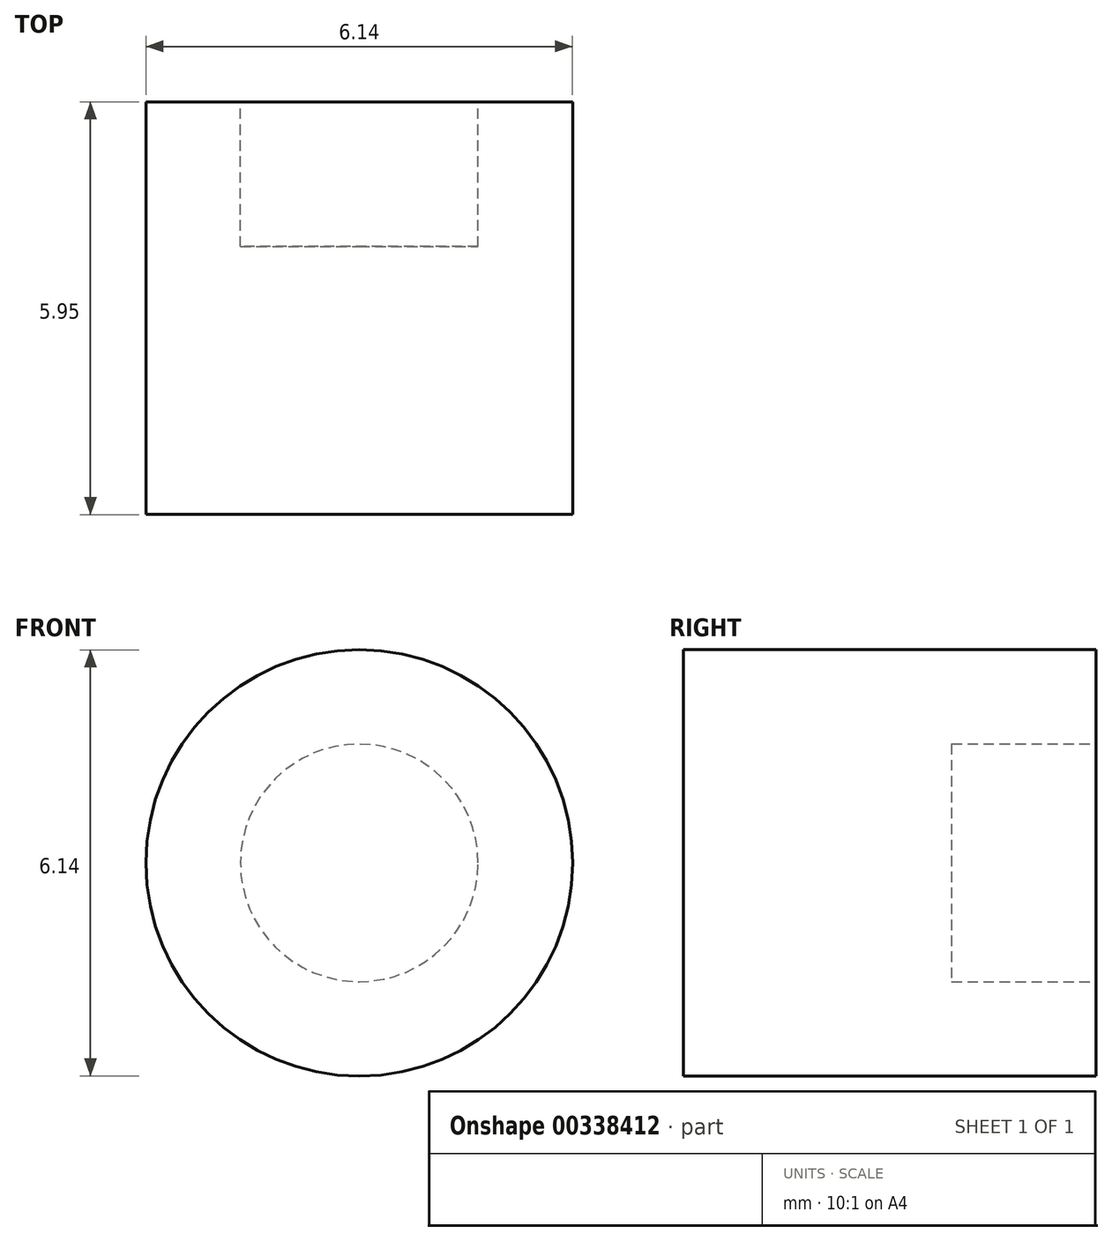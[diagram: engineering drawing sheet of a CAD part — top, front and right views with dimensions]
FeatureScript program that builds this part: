
annotation { "Feature Type Name" : "Feature", "Feature Type Description" : "" }
export const myFeature = defineFeature(function(context is Context, id is Id, definition is map)
    precondition{}
    {
        {
            var Q0;
            Q0=qCreatedBy(makeId("Top.planeOp"),FACE);
            var sketch = newSketch(context, id + "F0", { "sketchPlane" : qUnion([Q0])});
            skLineSegment(sketch, "E0.bottom", {"start": v(0.66, 0.45) * mm, "end": v(3.73, 0.45) * mm});
            skLineSegment(sketch, "E0.top", {"start": v(0.66, -5.5) * mm, "end": v(3.73, -5.5) * mm});
            skLineSegment(sketch, "E0.left", {"start": v(0.66, 0.45) * mm, "end": v(0.66, -5.5) * mm});
            skLineSegment(sketch, "E0.right", {"start": v(3.73, 0.45) * mm, "end": v(3.73, -5.5) * mm});
            skLineSegment(sketch, "E1", {"start": v(0.66, -5.5) * mm, "end": v(3.73, -5.5) * mm, "construction": true});
            skLineSegment(sketch, "E2", {"start": v(3.73, 0.45) * mm, "end": v(3.73, -5.5) * mm, "construction": true});
            skSolve(sketch);
        }
        {
            var Q0;
            Q0=makeQuery(id+"F0.imprint","IMPRINT",FACE,{"disambiguationData":[TD([[makeQuery(id+"F0.imprint","IMPRINT",EDGE,{"derivedFrom":sQuery(id+"F0.wireOp",EDGE,"E0.bottom")}),-1.0]])]});
            var Q1;
            Q1=sQuery(id+"F0.wireOp",EDGE,"E0.right");
            revolve(context, id + "F1", {"entities" : qUnion([Q0]), "axis" : qUnion([Q1]), "revolveType" : RevolveType.FULL});
        }
        {
            var Q0;
            Q0=makeQuery(id+"F1.opRevolve","SWEPT_FACE",FACE,{"disambiguationData":[OSD([sQuery(id+"F0.wireOp",EDGE,"E0.bottom")])]});
            var sketch = newSketch(context, id + "F2", { "sketchPlane" : qUnion([Q0])});
            skCircle(sketch, "E3", {"center": v(-3.73, 0) * mm, "radius": 1.71 * mm});
            skSolve(sketch);
        }
        {
            var Q0;
            Q0 = qSketchRegion(id + "F2", true);
            extrude(context, id + "F3", {"entities" : qUnion([Q0]), "operationType" : NewBodyOperationType.REMOVE, "oppositeDirection" : true, "depth" : 2.08 * mm});
        }
    });
